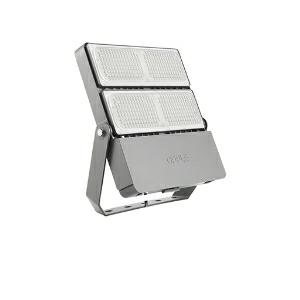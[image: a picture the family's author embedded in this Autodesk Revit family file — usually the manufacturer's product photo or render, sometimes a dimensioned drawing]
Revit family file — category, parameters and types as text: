
# Revit family: ledfloodmo-p_re450-200w-857-n_709000058800
name_source: partatom
category: Leuchten
revit_build: Autodesk Revit 2016 (Build: 20190508_0715(x64)
units: mm (PartAtom-declared; Revit-internal decimal feet)

## family parameters
Basisbauteil = Fläche
Beim Laden mit Abzugskörper schneiden = Nein
Bemaßung runder Anschluss = Durchmesser verwenden
Gemeinsam genutzt = Nein
Lichtquelle = Nein
Raumberechnungspunkt = Nein
Teiletyp = Normal

## types (1)
- LEDFloodMo-P Re450-200W-857-N (1 x LED, 28000 lm)
    Approval mark = CE
    Beschreibung = Precise modular optical design for area, object and facade lighting. Super slim aluminium body with integrated heatsink. Robust design with high protection against water and dust. High energy saving up to 65% compared to halogen and high pressure sodium lamps. IP66 and suitable for use on the coastal applications.
    CIE Flux Codes = 81 94 99 99 100
    Control Gear = Electronic ballast
    Height = 54 mm
    Hersteller = OPPLE
    Lamp Light Flux = 28000 lm
    Lamp count = 1
    Lampe = 1 x LED
    Length = 396 mm
    Luminous efficacy = 140 lm/W
    ModVariant = Nein
    Modell = 709000058800
    Mounting Place = Pole
    Mounting Type = Pole top
    Number of Poles = 1
    OnlyDefault = Ja
    Power Factor = 1
    Product Name = LEDFloodMo-P Re450-200W-857-N
    Product group = Floodlight Modulo Performer
    ProductGroupID = 2006
    Protection Class = Protection class I
    Protection Degree = IP 66
    RLX_Detail_Level = 1
    RlxData = <blob elided: 177129 chars, md5=ce037603>
    Scheinlast = 200 VA
    Socket = socket
    Standby Power = 0 W
    System Light Flux = 27972 lm
    System Power = 200 W
    Typenbild = modulo_re450.jpg
    Typenkommentare = Product without accessories
    URL = http://relux.com
    VarID = ---
    Voltage = 230 V
    Voltage Range = 220-240 V
    Vorgabe-Ansicht = 1800 mm
    Weight = 0.00 kg
    Width = 400 mm

## geometry (parser evidence)
native form markers: Sweep x11
no freeform markers — native parametric forms only
